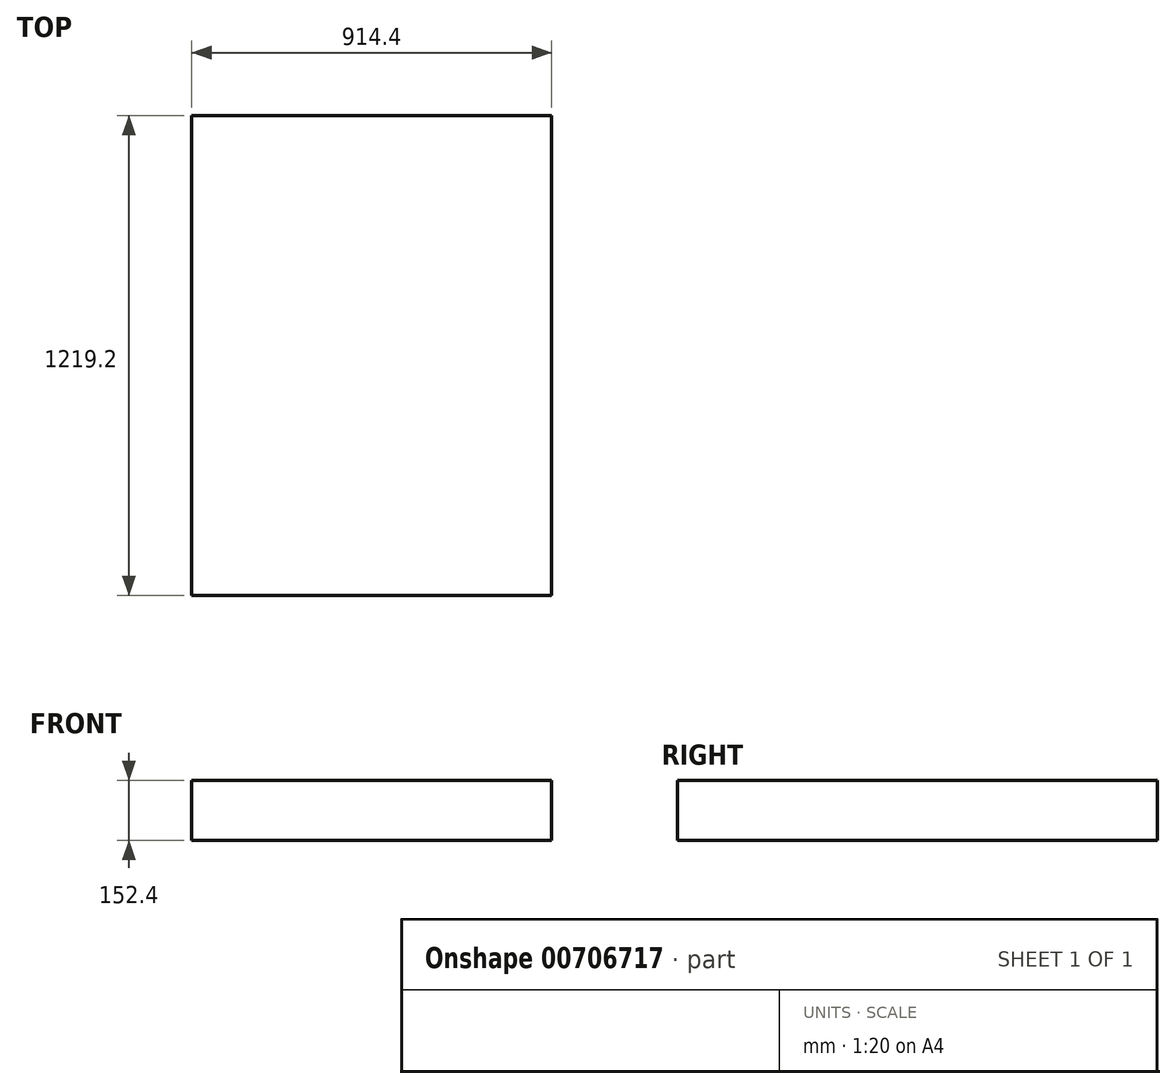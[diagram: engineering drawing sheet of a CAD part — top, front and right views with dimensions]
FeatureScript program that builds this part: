
annotation { "Feature Type Name" : "Feature", "Feature Type Description" : "" }
export const myFeature = defineFeature(function(context is Context, id is Id, definition is map)
    precondition{}
    {
        {
            var Q0;
            Q0=qCreatedBy(makeId("Top.planeOp"),FACE);
            var sketch = newSketch(context, id + "F0", { "sketchPlane" : qUnion([Q0])});
            skLineSegment(sketch, "E0.bottom", {"start": v(0, 0) * mm, "end": v(914.4, 0) * mm});
            skLineSegment(sketch, "E0.top", {"start": v(0, 1219.2) * mm, "end": v(914.4, 1219.2) * mm});
            skLineSegment(sketch, "E0.left", {"start": v(0, 0) * mm, "end": v(0, 1219.2) * mm});
            skLineSegment(sketch, "E0.right", {"start": v(914.4, 0) * mm, "end": v(914.4, 1219.2) * mm});
            skSolve(sketch);
        }
        {
            var Q0;
            Q0=makeQuery(id+"F0.imprint","IMPRINT",FACE,{"disambiguationData":[TD([[makeQuery(id+"F0.imprint","IMPRINT",EDGE,{"derivedFrom":sQuery(id+"F0.wireOp",EDGE,"E0.bottom")}),1.0]])]});
            extrude(context, id + "F1", {"entities" : qUnion([Q0]), "depth" : 152.4 * mm, "offsetDistance" : 25.4 * mm});
        }
    });
